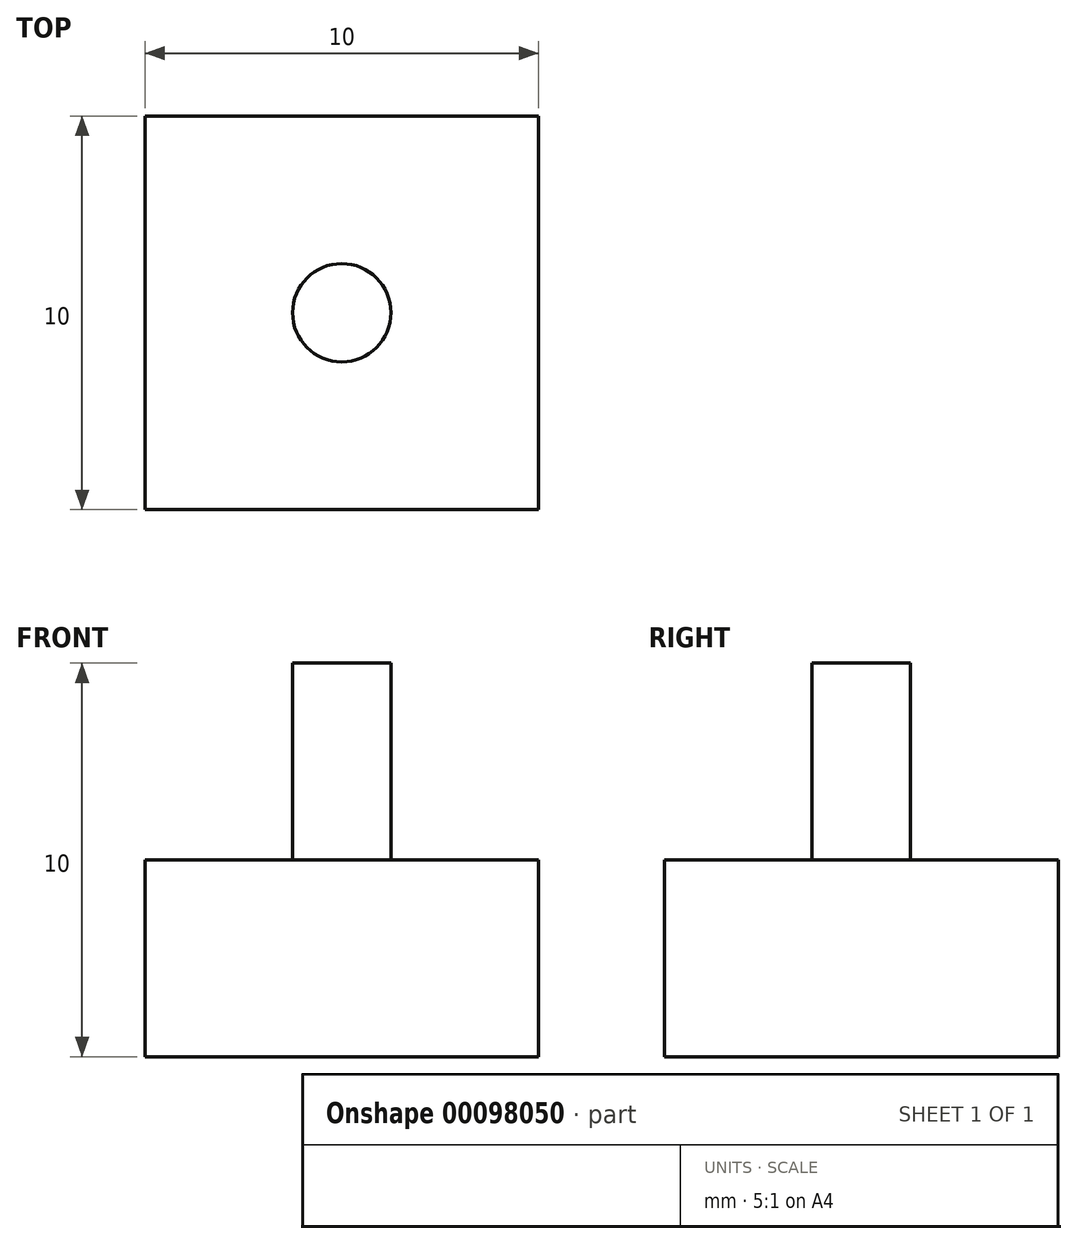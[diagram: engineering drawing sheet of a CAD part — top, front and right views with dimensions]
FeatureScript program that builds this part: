
annotation { "Feature Type Name" : "Feature", "Feature Type Description" : "" }
export const myFeature = defineFeature(function(context is Context, id is Id, definition is map)
    precondition{}
    {
        {
            var Q0;
            Q0=qCreatedBy(makeId("Top.planeOp"),FACE);
            var sketch = newSketch(context, id + "F0", { "sketchPlane" : qUnion([Q0])});
            skLineSegment(sketch, "E0.bottom", {"start": v(0, 0) * mm, "end": v(10, 0) * mm});
            skLineSegment(sketch, "E0.top", {"start": v(0, 10) * mm, "end": v(10, 10) * mm});
            skLineSegment(sketch, "E0.left", {"start": v(0, 0) * mm, "end": v(0, 10) * mm});
            skLineSegment(sketch, "E0.right", {"start": v(10, 0) * mm, "end": v(10, 10) * mm});
            skSolve(sketch);
        }
        {
            var Q0;
            Q0 = qSketchRegion(id + "F0", true);
            extrude(context, id + "F1", {"entities" : qUnion([Q0]), "depth" : 5 * mm});
        }
        {
            var Q0;
            Q0=makeQuery(id+"F1.opExtrude","CAP_FACE",FACE,{"disambiguationData":[OSD([sQuery(id+"F0.wireOp",EDGE,"E0.bottom"),sQuery(id+"F0.wireOp",EDGE,"E0.top"),sQuery(id+"F0.wireOp",EDGE,"E0.left"),sQuery(id+"F0.wireOp",EDGE,"E0.right")])],"isStart":false});
            var sketch = newSketch(context, id + "F2", { "sketchPlane" : qUnion([Q0])});
            skCircle(sketch, "E1", {"center": v(5, 5) * mm, "radius": 1.25 * mm});
            skSolve(sketch);
        }
        {
            var Q0;
            Q0 = qSketchRegion(id + "F2", true);
            extrude(context, id + "F3", {"entities" : qUnion([Q0]), "operationType" : NewBodyOperationType.ADD, "depth" : 5 * mm});
        }
    });
